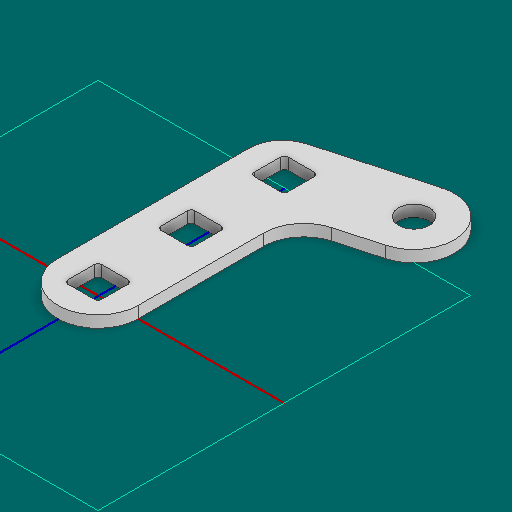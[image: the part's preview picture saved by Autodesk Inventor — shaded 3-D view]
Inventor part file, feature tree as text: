
AUTODESK INVENTOR PART (.ipt)
format: ipt  version: 2025 (Build 290162000, 162)  size: 138,752 bytes
history: native  units: in
note: dims shown in document units (in); Inventor stores cm internally (conversion verified against a paired STEP export)
features: other x3, extrude x1, sketch x1
ambient origin geometry x8: Origin, YZ Plane, XZ Plane, XY Plane, X Axis, Y Axis, Z Axis, Center Point
bodies: Solid1 (feature_tree)
feature tree (5):
  other  "Blocks"
  extrude  "Extrusion1"  [1 undecoded]
  sketch  "Sketch1"  dims[d0=0.0625in d1=0.0in]
  other  "main"
  other  "main:1"
note: 1 required parameter value undecoded (feature->parameter linkage not recoverable at this tier; creation-order binding heuristic only, values carry confidence <= 0.55)
